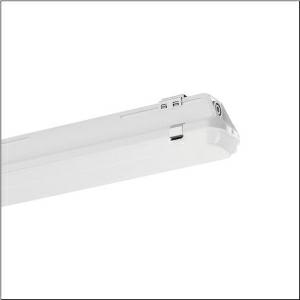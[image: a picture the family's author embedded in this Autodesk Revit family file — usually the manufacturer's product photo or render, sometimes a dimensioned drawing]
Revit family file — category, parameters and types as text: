
# Revit family: monsun_21_51fb207p430k
name_source: partatom
category: Lighting Fixtures
units: mm (PartAtom-declared; Revit-internal decimal feet)

## family parameters
Cut with Voids When Loaded = No
Host = Face
Light Source = No
Part Type = Normal
Room Calculation Point = No
Round Connector Dimension = Use Diameter
Shared = No

## types (1)
- Monsun 21 (1 x LED, 3550 lm, 22.1 W, 4000K)
    Apparent Load = 22 VA
    CIE Flux Codes = 45 75 93 94 100
    Color Rendering = 80
    Color Temperature = 4000K
    Default Elevation = 1800 mm
    Description = Monsun 21, damp-proof luminaire, chain hanger, primary optical cover: enclosure, of PC, light emission: direct distribution, primary light characteristic: symmetric, installation type: suspended mounting, surface-mounted, horizontal mounting, vertical mounting, LED, rated luminous flux: 3.550lm, luminous efficacy: 161lm/W, light colour: 840, colour temperature: 4000K, control gear: ON/OFF, with terminal, 3-pole, max. 2.5mm², mains connection: 220..240V, AC, 50/60Hz, rated input power: 22W, housing, of glass-fibre reinforced polyester, uncoated, bright grey, incl. chain hanger, length: 1.590mm, width: 90mm, height: 88mm, clip for enclosure, of stainless steel (V2A), ceiling mounting element, of stainless steel (V2A), chain hanger, of stainless steel (V2A), protection rating (complete): IP66, insulation class (complete): insulation class I (protective earthing), certification: CE, ENEC, VDE, UKCA, protection symbol: D, impact resistance: IK08, permissible operating ambient temperature: -25..+35°C, standard: EN 50419, EN 60598-2-1, corresponds to IFS (International Featured Standards) requirements for safety and quality in the food industry, for indoor or canopied outdoor use, no direct snow, no direct sun, no direct rain, LABS conformity tested according to VDMA 24364:2018-05, contact your sales advisor before using the luminaires in applications with unclear chemical exposure, large temperature fluctuations or condensation-forming humidity, packaging unit: 1 piece
    Height = 89 mm
    Lamp = 1 x LED
    Lamp Light Flux = 3550 lm
    Lamp Power = 22.1 W
    Lamp count = 1
    Length = 1590 mm
    Luminous efficacy = 161 lm/W
    Manufacturer = Siteco
    ModVariant = No
    Model = 51FB207P430K
    Mounting Place = Ceiling
    Mounting Type = Surface mounted
    Number of Poles = 1
    OnlyDefault = Yes
    Power Factor = 1
    Product Name = Monsun 21
    Product group = damp-proof luminaire
    ProductGroupID = 300
    Protection Class = Protection class I
    Protection Degree = IP 66
    RLX_Detail_Level = 1
    RLX_Emergency_Light_Flux = 0 lm
    RLX_Emergency_Type = 0
    RLX_Emergency_Type_DB = No
    RlxData = <blob elided: 88729 chars, md5=611c1456>
    Socket = socket
    Standby Power = 0 W
    System Light Flux = 3550 lm
    System Power = 22 W
    Type Comments = Product without accessories
    Type Image = l_1319656.jpg
    URL = http://relux.com
    VarID = ---
    Voltage = 0 V
    Weight = 0.00 kg
    Width = 90 mm

## geometry (parser evidence)
native form markers: Blend x4, Sweep x13
no freeform markers — native parametric forms only
